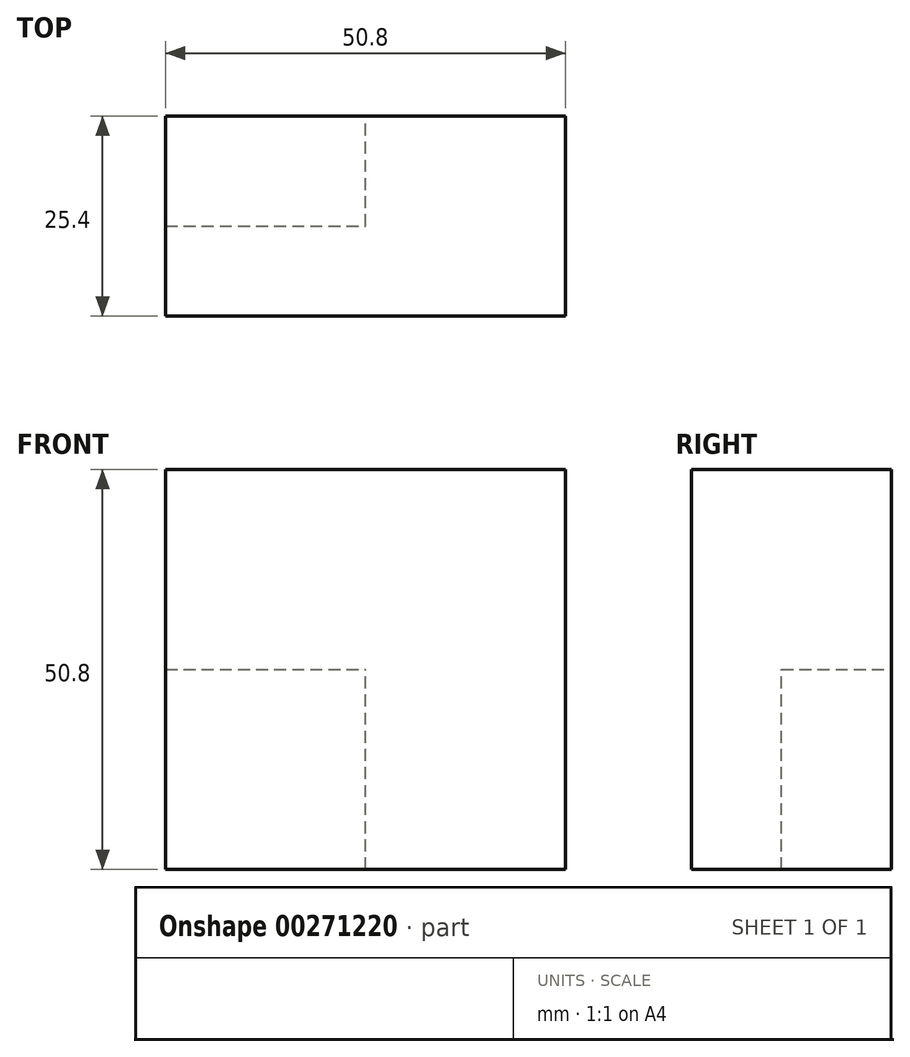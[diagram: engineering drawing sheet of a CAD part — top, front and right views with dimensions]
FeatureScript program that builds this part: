
annotation { "Feature Type Name" : "Feature", "Feature Type Description" : "" }
export const myFeature = defineFeature(function(context is Context, id is Id, definition is map)
    precondition{}
    {
        {
            var Q0;
            Q0=qCreatedBy(makeId("Front.planeOp"),FACE);
            var sketch = newSketch(context, id + "F0", { "sketchPlane" : qUnion([Q0])});
            skLineSegment(sketch, "E0.bottom", {"start": v(0, 0) * mm, "end": v(50.8, 0) * mm});
            skLineSegment(sketch, "E0.top", {"start": v(0, 50.8) * mm, "end": v(50.8, 50.8) * mm});
            skLineSegment(sketch, "E0.left", {"start": v(0, 0) * mm, "end": v(0, 50.8) * mm});
            skLineSegment(sketch, "E0.right", {"start": v(50.8, 0) * mm, "end": v(50.8, 50.8) * mm});
            skSolve(sketch);
        }
        {
            var Q0;
            Q0=makeQuery(id+"F0.imprint","IMPRINT",FACE,{"disambiguationData":[TD([[makeQuery(id+"F0.imprint","IMPRINT",EDGE,{"derivedFrom":sQuery(id+"F0.wireOp",EDGE,"E0.bottom")}),1.0]])]});
            extrude(context, id + "F1", {"entities" : qUnion([Q0]), "depth" : 25.4 * mm});
        }
        {
            var Q0;
            Q0=qCreatedBy(makeId("Front.planeOp"),FACE);
            var sketch = newSketch(context, id + "F2", { "sketchPlane" : qUnion([Q0])});
            skLineSegment(sketch, "E1.bottom", {"start": v(0, 0) * mm, "end": v(25.4, 0) * mm});
            skLineSegment(sketch, "E1.top", {"start": v(0, 25.4) * mm, "end": v(25.4, 25.4) * mm});
            skLineSegment(sketch, "E1.left", {"start": v(0, 0) * mm, "end": v(0, 25.4) * mm});
            skLineSegment(sketch, "E1.right", {"start": v(25.4, 0) * mm, "end": v(25.4, 25.4) * mm});
            skSolve(sketch);
        }
        {
            var Q0;
            Q0=makeQuery(id+"F2.imprint","IMPRINT",FACE,{"disambiguationData":[TD([[makeQuery(id+"F2.imprint","IMPRINT",EDGE,{"derivedFrom":sQuery(id+"F2.wireOp",EDGE,"E1.bottom")}),1.0]])]});
            extrude(context, id + "F3", {"entities" : qUnion([Q0]), "operationType" : NewBodyOperationType.REMOVE, "depth" : 13.97 * mm});
        }
    });
